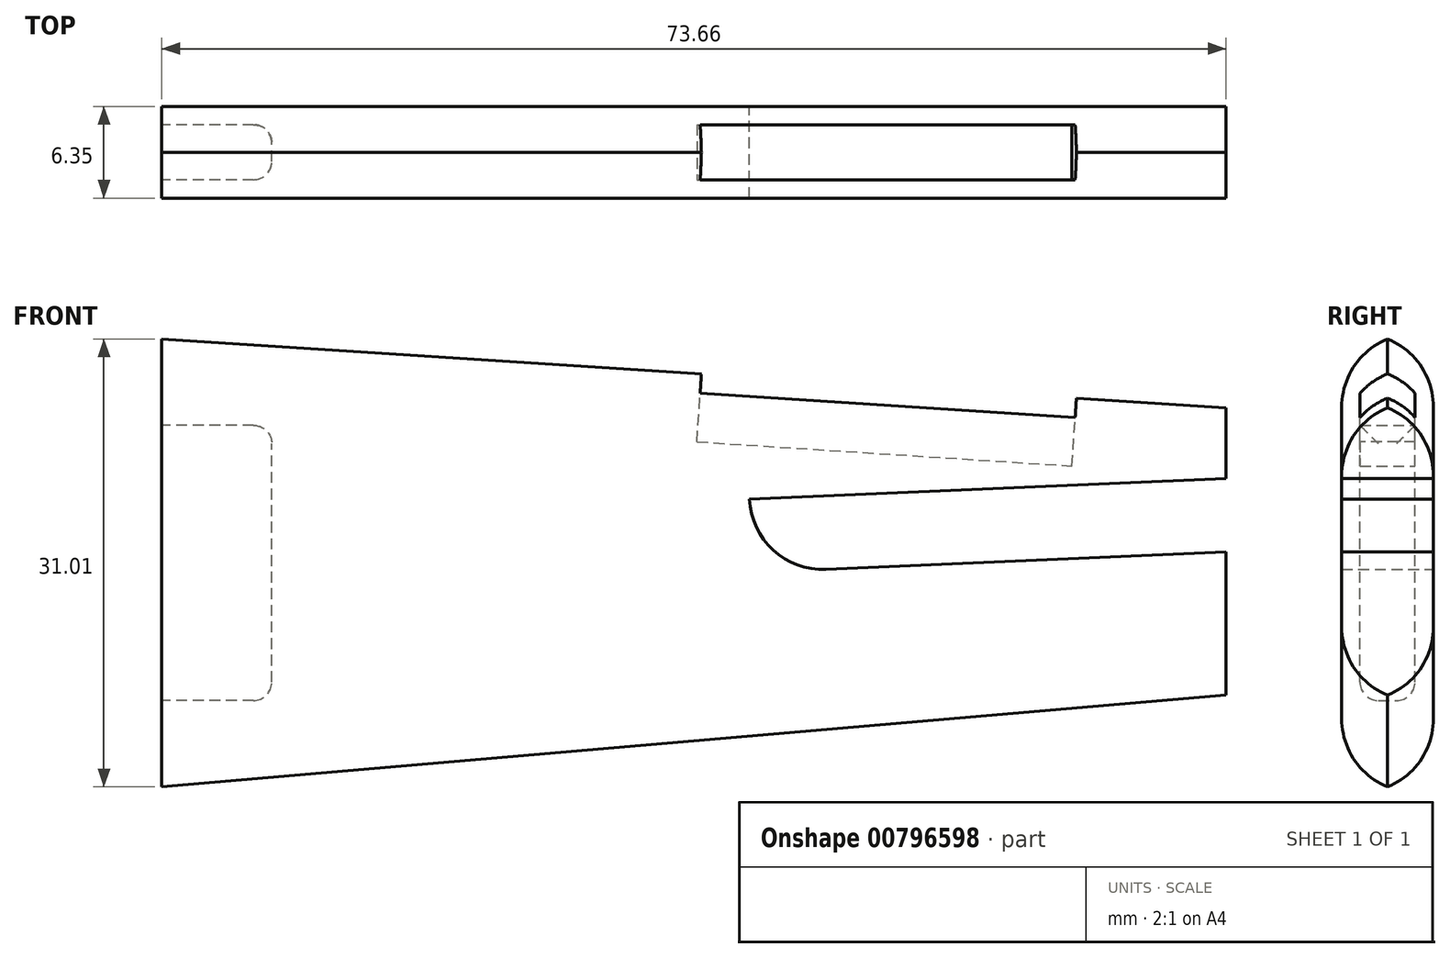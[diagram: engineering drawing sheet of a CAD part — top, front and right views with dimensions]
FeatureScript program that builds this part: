
annotation { "Feature Type Name" : "Feature", "Feature Type Description" : "" }
export const myFeature = defineFeature(function(context is Context, id is Id, definition is map)
    precondition{}
    {
        {
            var Q0;
            Q0=qCreatedBy(makeId("Front.planeOp"),FACE);
            var sketch = newSketch(context, id + "F0", { "sketchPlane" : qUnion([Q0])});
            skLineSegment(sketch, "E0", {"start": v(28.88, 12.88) * mm, "end": v(-44.78, 17.64) * mm});
            skLineSegment(sketch, "E1", {"start": v(28.88, 2.53) * mm, "end": v(-3.89, 1.1) * mm});
            skLineSegment(sketch, "E2", {"start": v(-44.78, 17.64) * mm, "end": v(-44.78, -14.1) * mm});
            skLineSegment(sketch, "E3", {"start": v(28.88, 12.88) * mm, "end": v(28.88, -7.76) * mm});
            skLineSegment(sketch, "E4", {"start": v(-4.1, 6.18) * mm, "end": v(-3.89, 1.1) * mm});
            skLineSegment(sketch, "E5", {"start": v(-4.1, 6.18) * mm, "end": v(28.88, 7.62) * mm});
            skLineSegment(sketch, "E6", {"start": v(-44.78, -14.1) * mm, "end": v(28.88, -7.76) * mm});
            skSolve(sketch);
        }
        {
            var Q0;
            {var subQ1=sQuery(id+"F0.wireOp",EDGE,"E0");Q0=makeQuery(id+"F0.imprint","IMPRINT",FACE,{"disambiguationData":[TD([[makeQuery(id+"F0.imprint","IMPRINT",EDGE,{"derivedFrom":subQ1}),1.0]])]});}
            extrude(context, id + "F1", {"entities" : qUnion([Q0]), "depth" : 6.35 * mm, "offsetDistance" : 25.4 * mm});
        }
        {
            var Q0;
            Q0=makeQuery(id+"F1.opExtrude","SWEPT_FACE",FACE,{"disambiguationData":[OSD([sQuery(id+"F0.wireOp",EDGE,"E2")])]});
            var sketch = newSketch(context, id + "F2", { "sketchPlane" : qUnion([Q0])});
            skLineSegment(sketch, "E7.0.0", {"start": v(0, 17.64) * mm, "end": v(0, 17.64) * mm});
            skLineSegment(sketch, "E7.0.1", {"start": v(6.35, 17.64) * mm, "end": v(0, 17.64) * mm});
            skLineSegment(sketch, "E7.0.2", {"start": v(6.35, 17.64) * mm, "end": v(6.35, 17.64) * mm});
            skLineSegment(sketch, "E7.0.3", {"start": v(6.35, 17.64) * mm, "end": v(0, 17.64) * mm});
            skPoint(sketch, "E8.0", {"position": v(0, 6.18) * mm});
            skPoint(sketch, "E9.startSnap0", {"position": v(3.18, 17.64) * mm});
            skPoint(sketch, "E9.startSnap1", {"position": v(6.35, 1.77) * mm});
            skLineSegment(sketch, "E10.bottom", {"start": v(5.08, -7.76) * mm, "end": v(1.27, -7.76) * mm});
            skLineSegment(sketch, "E10.top", {"start": v(5.08, 11.3) * mm, "end": v(1.27, 11.3) * mm});
            skLineSegment(sketch, "E10.left", {"start": v(5.08, -7.76) * mm, "end": v(5.08, 11.3) * mm});
            skLineSegment(sketch, "E10.right", {"start": v(1.27, -7.76) * mm, "end": v(1.27, 11.3) * mm});
            skPoint(sketch, "E10.middle", {"position": v(3.18, 1.77) * mm});
            skSolve(sketch);
        }
        {
            var Q0;
            Q0=makeQuery(id+"F2.imprint","IMPRINT",FACE,{"disambiguationData":[TD([[makeQuery(id+"F2.imprint","IMPRINT",EDGE,{"derivedFrom":sQuery(id+"F2.wireOp",EDGE,"E10.bottom")}),-1.0]])]});
            extrude(context, id + "F3", {"entities" : qUnion([Q0]), "operationType" : NewBodyOperationType.REMOVE, "oppositeDirection" : true, "depth" : 7.62 * mm, "offsetDistance" : 25.4 * mm});
        }
        {
            var Q0;
            Q0=makeQuery(id+"F3.boolean.opBoolean","COPY",EDGE,{"derivedFrom":makeQuery(id+"F3.opExtrude","CAP_EDGE",EDGE,{"disambiguationData":[OSD([sQuery(id+"F2.wireOp",EDGE,"E10.bottom")])],"isStart":false})});
            fillet(context, id + "F4", {"entities" : qUnion([Q0]), "radius" : 1.27 * mm, "tangentPropagation" : true, "allowEdgeOverflow" : false});
        }
        {
            var Q0;
            Q0=makeQuery(id+"F3.boolean.opBoolean","COPY",EDGE,{"derivedFrom":makeQuery(id+"F3.opExtrude","CAP_EDGE",EDGE,{"disambiguationData":[OSD([sQuery(id+"F2.wireOp",EDGE,"E10.top")])],"isStart":false})});
            var Q1;
            Q1=makeQuery(id+"F3.boolean.opBoolean","COPY",EDGE,{"derivedFrom":makeQuery(id+"F3.opExtrude","CAP_EDGE",EDGE,{"disambiguationData":[OSD([sQuery(id+"F2.wireOp",EDGE,"E10.left")])],"isStart":false})});
            var Q2;
            Q2=makeQuery(id+"F3.boolean.opBoolean","COPY",EDGE,{"derivedFrom":makeQuery(id+"F3.opExtrude","CAP_EDGE",EDGE,{"disambiguationData":[OSD([sQuery(id+"F2.wireOp",EDGE,"E10.right")])],"isStart":false})});
            fillet(context, id + "F5", {"entities" : qUnion([Q0, Q1, Q2]), "radius" : 1.27 * mm, "tangentPropagation" : true, "allowEdgeOverflow" : false});
        }
        {
            var Q0;
            Q0=makeQuery(id+"F1.opExtrude","SWEPT_FACE",FACE,{"disambiguationData":[OSD([sQuery(id+"F0.wireOp",EDGE,"E0")])]});
            var sketch = newSketch(context, id + "F6", { "sketchPlane" : qUnion([Q0])});
            skLineSegment(sketch, "E11.0.0", {"start": v(28, 0) * mm, "end": v(-45.82, 0) * mm});
            skLineSegment(sketch, "E11.0.1", {"start": v(-45.82, 0) * mm, "end": v(-45.82, -6.35) * mm});
            skLineSegment(sketch, "E11.0.2", {"start": v(-45.82, -6.35) * mm, "end": v(28, -6.35) * mm});
            skLineSegment(sketch, "E11.0.3", {"start": v(28, -6.35) * mm, "end": v(28, 0) * mm});
            skLineSegment(sketch, "E12", {"start": v(2.6, -1.27) * mm, "end": v(-8.38, -1.27) * mm});
            skLineSegment(sketch, "E13", {"start": v(-8.38, -5.08) * mm, "end": v(15.3, -5.08) * mm});
            skLineSegment(sketch, "E14", {"start": v(2.6, -1.27) * mm, "end": v(15.3, -1.27) * mm});
            skLineSegment(sketch, "E15", {"start": v(15.3, -5.08) * mm, "end": v(17.63, -5.08) * mm});
            skLineSegment(sketch, "E16", {"start": v(17.63, -5.08) * mm, "end": v(17.63, -1.27) * mm});
            skLineSegment(sketch, "E17", {"start": v(17.63, -1.27) * mm, "end": v(15.3, -1.27) * mm});
            skLineSegment(sketch, "E18", {"start": v(-8.38, -1.27) * mm, "end": v(-8.38, -5.08) * mm});
            skSolve(sketch);
        }
        {
            var Q0;
            Q0=makeQuery(id+"F6.imprint","IMPRINT",FACE,{"disambiguationData":[TD([[makeQuery(id+"F6.imprint","IMPRINT",EDGE,{"derivedFrom":sQuery(id+"F6.wireOp",EDGE,"E12")}),1.0]])]});
            extrude(context, id + "F7", {"entities" : qUnion([Q0]), "operationType" : NewBodyOperationType.REMOVE, "oppositeDirection" : true, "depth" : 5.08 * mm, "offsetDistance" : 25.4 * mm});
        }
        {
            var Q0;
            Q0=makeQuery(id+"F1.opExtrude","CAP_EDGE",EDGE,{"disambiguationData":[OSD([sQuery(id+"F0.wireOp",EDGE,"E6")])],"isStart":false});
            var Q1;
            Q1=makeQuery(id+"F1.opExtrude","CAP_EDGE",EDGE,{"disambiguationData":[OSD([sQuery(id+"F0.wireOp",EDGE,"E6")])],"isStart":true});
            var Q2;
            Q2=makeQuery(id+"F1.opExtrude","CAP_EDGE",EDGE,{"disambiguationData":[OSD([sQuery(id+"F0.wireOp",EDGE,"E0")])],"isStart":false});
            var Q3;
            Q3=makeQuery(id+"F1.opExtrude","CAP_EDGE",EDGE,{"disambiguationData":[OSD([sQuery(id+"F0.wireOp",EDGE,"E0")])],"isStart":true});
            fillet(context, id + "F8", {"entities" : qUnion([Q0, Q1, Q2, Q3]), "radius" : 5.08 * mm, "tangentPropagation" : true, "allowEdgeOverflow" : false});
        }
        {
            var Q0;
            Q0=makeQuery(id+"F1.opExtrude","SWEPT_EDGE",EDGE,{"disambiguationData":[OSD([sQuery(id+"F0.wireOp",EDGE,"E1"),sQuery(id+"F0.wireOp",EDGE,"E4")])]});
            fillet(context, id + "F9", {"entities" : qUnion([Q0]), "radius" : 5.08 * mm, "tangentPropagation" : true, "allowEdgeOverflow" : false});
        }
    });
